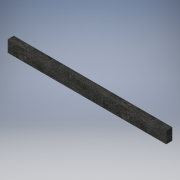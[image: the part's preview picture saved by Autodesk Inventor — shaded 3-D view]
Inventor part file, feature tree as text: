
AUTODESK INVENTOR PART (.ipt)
format: ipt  version: 2019 (Build 230136000, 136)  size: 102,912 bytes
history: native  units: mm
features: extrude x1, sketch x1
ambient origin geometry x8: Origin, YZ Plane, XZ Plane, XY Plane, X Axis, Y Axis, Z Axis, Center Point
bodies: Solid1 (feature_tree)
feature tree (2):
  extrude  "Extrusion1"  Depth=20.0mm
  sketch  "Sketch1"  dims[d0=270.0mm d1=20.0mm d2=217.645673mm d3=10.0mm d4=10.0mm d5=0.0mm]
